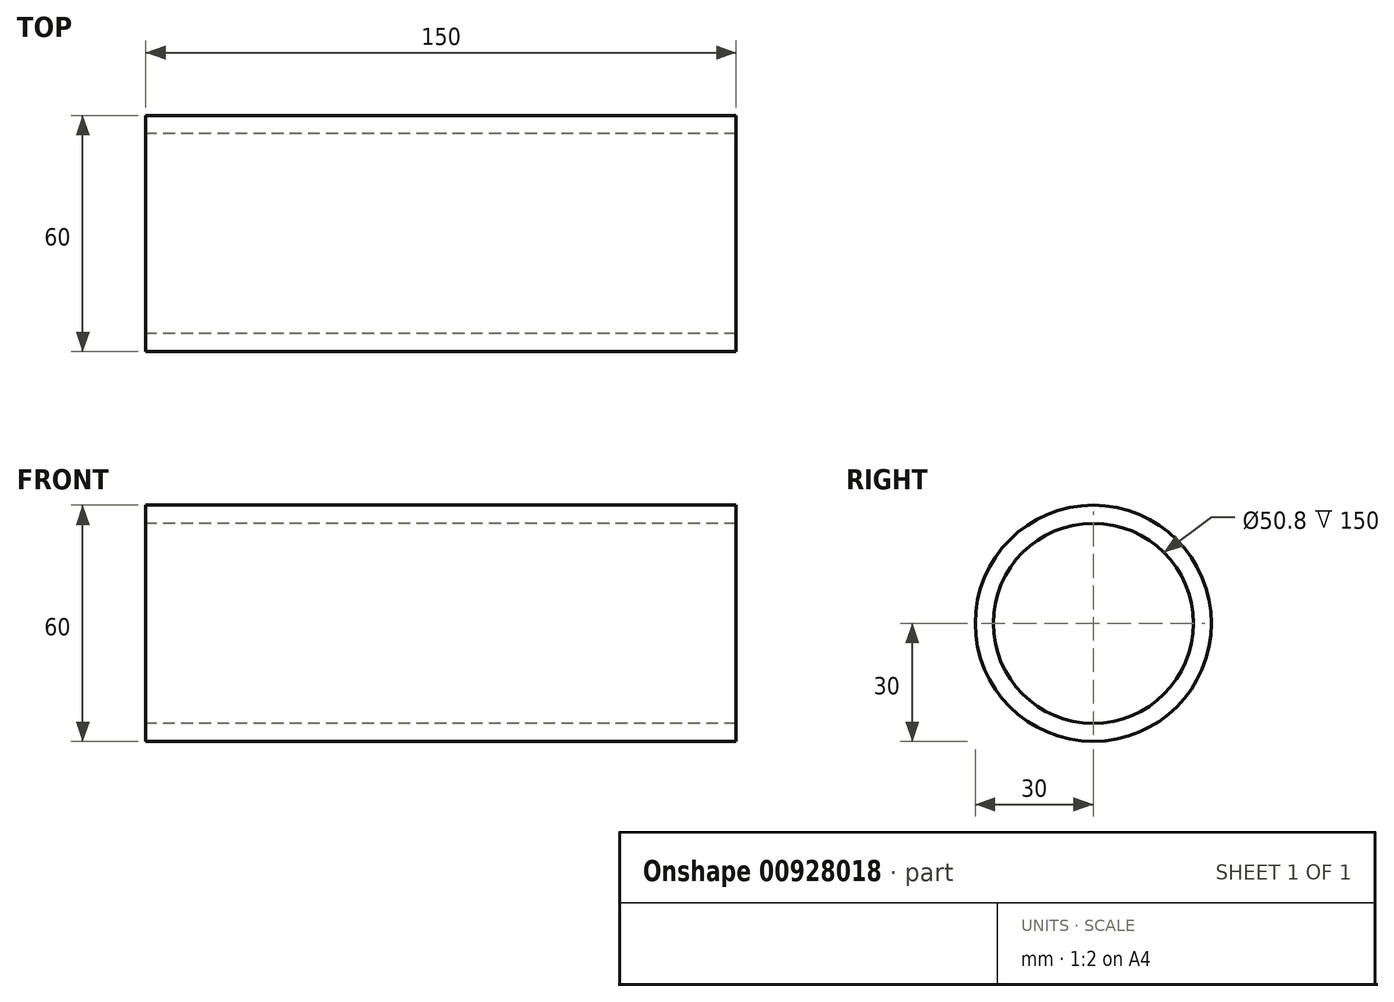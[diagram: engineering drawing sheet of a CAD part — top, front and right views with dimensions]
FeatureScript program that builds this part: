
annotation { "Feature Type Name" : "Feature", "Feature Type Description" : "" }
export const myFeature = defineFeature(function(context is Context, id is Id, definition is map)
    precondition{}
    {
        {
            var Q0;
            Q0=qCreatedBy(makeId("Right.planeOp"),FACE);
            var sketch = newSketch(context, id + "F0", { "sketchPlane" : qUnion([Q0])});
            skCircle(sketch, "E0", {"center": v(0, 0) * mm, "radius": 30 * mm});
            skCircle(sketch, "E1", {"center": v(0, 0) * mm, "radius": 25.4 * mm});
            skSolve(sketch);
        }
        {
            var Q0;
            Q0=qSketchRegion(id+"F0",true);
            extrude(context, id + "F1", {"entities" : qUnion([Q0]), "depth" : 150 * mm, "offsetDistance" : 25 * mm});
        }
    });
